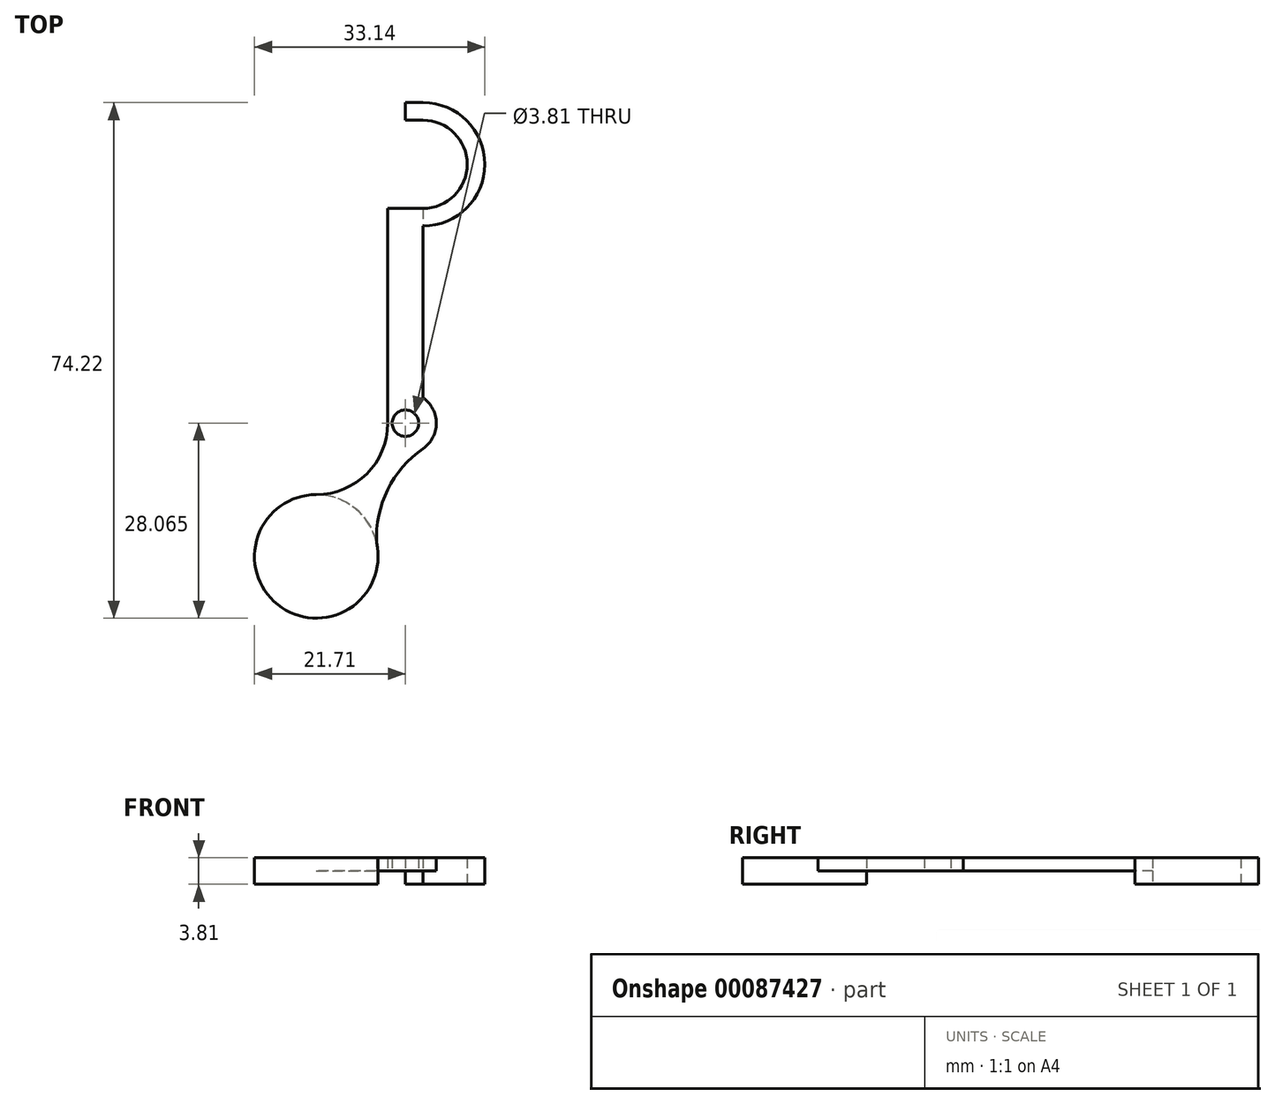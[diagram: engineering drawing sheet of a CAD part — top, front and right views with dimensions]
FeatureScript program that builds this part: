
annotation { "Feature Type Name" : "Feature", "Feature Type Description" : "" }
export const myFeature = defineFeature(function(context is Context, id is Id, definition is map)
    precondition{}
    {
        {
            var Q0;
            Q0=qCreatedBy(makeId("Top.planeOp"),FACE);
            var sketch = newSketch(context, id + "F0", { "sketchPlane" : qUnion([Q0])});
            skLineSegment(sketch, "E0", {"start": v(0, 50.8) * mm, "end": v(0, 0) * mm, "construction": true});
            skLineSegment(sketch, "E1", {"start": v(0, 35.56) * mm, "end": v(0, 0) * mm});
            skPoint(sketch, "E2", {"position": v(-31.04, 0) * mm});
            skCircle(sketch, "E3", {"center": v(-15.36, -11.99) * mm, "radius": 8.9 * mm});
            skLineSegment(sketch, "E4", {"start": v(0, 53.34) * mm, "end": v(0, 50.8) * mm});
            skArc(sketch, "E5", {"start": v(-15.36, -3.1) * mm, "mid": v(-8.1, -0.09) * mm, "end": v(-5.08, 7.19) * mm});
            skArc(sketch, "E6", {"start": v(0, 35.56) * mm, "mid": v(8.89, 44.45) * mm, "end": v(0, 53.34) * mm});
            skArc(sketch, "E7", {"start": v(0, 38.1) * mm, "mid": v(6.35, 44.45) * mm, "end": v(0, 50.8) * mm});
            skLineSegment(sketch, "E8", {"start": v(0, 38.1) * mm, "end": v(0, 35.56) * mm});
            skLineSegment(sketch, "E9", {"start": v(-5.08, 38.1) * mm, "end": v(0, 38.1) * mm});
            skLineSegment(sketch, "E10", {"start": v(-5.08, 38.1) * mm, "end": v(-5.08, 0) * mm});
            skLineSegment(sketch, "E11", {"start": v(0, 3.54) * mm, "end": v(-5.08, 0) * mm, "construction": true});
            skLineSegment(sketch, "E12", {"start": v(0, 53.34) * mm, "end": v(-2.54, 53.34) * mm});
            skLineSegment(sketch, "E13", {"start": v(-2.54, 53.34) * mm, "end": v(-2.54, 50.8) * mm});
            skLineSegment(sketch, "E14", {"start": v(-2.54, 50.8) * mm, "end": v(0, 50.8) * mm});
            skCircle(sketch, "E15", {"center": v(-2.54, 7.19) * mm, "radius": 1.9 * mm});
            skPoint(sketch, "E15.centerSnap0", {"position": v(-2.54, 1.77) * mm});
            skArc(sketch, "E16.0", {"start": v(0, 3.54) * mm, "mid": v(1.9, 7.19) * mm, "end": v(0, 10.83) * mm});
            skArc(sketch, "E17", {"start": v(0, 3.54) * mm, "mid": v(-5.5, -3.28) * mm, "end": v(-6.47, -11.99) * mm});
            skSolve(sketch);
        }
        {
            var Q0;
            Q0 = qSketchRegion(id + "F0", true);
            extrude(context, id + "F1", {"entities" : qUnion([Q0]), "depth" : 3.8 * mm});
        }
        {
            var Q0;
            {var subQ1=sQuery(id+"F0.wireOp",EDGE,"E1");Q0=makeQuery(id+"F0.imprint","IMPRINT",FACE,{"disambiguationData":[TD([[makeQuery(id+"F0.imprint","IMPRINT",EDGE,{"derivedFrom":subQ1}),-1.0]])]});}
            var Q1;
            {var subQ0=sQuery(id+"F0.wireOp",EDGE,"E5");Q1=makeQuery(id+"F0.imprint","IMPRINT",FACE,{"disambiguationData":[TD([[makeQuery(id+"F0.imprint","IMPRINT",EDGE,{"derivedFrom":subQ0}),-1.0]])]});}
            var Q2;
            {var subQ0=sQuery(id+"F0.wireOp",EDGE,"t0VB1PUQ-RfSN-Wfje-U51E-yYEwLlaeleKK");Q2=makeQuery(id+"F0.imprint","IMPRINT",FACE,{"disambiguationData":[TD([[makeQuery(id+"F0.imprint","IMPRINT",EDGE,{"derivedFrom":subQ0}),1.0]])]});}
            var Q3;
            {var subQ0=sQuery(id+"F0.wireOp",EDGE,"E16.0");Q3=makeQuery(id+"F0.imprint","IMPRINT",FACE,{"disambiguationData":[TD([[makeQuery(id+"F0.imprint","IMPRINT",EDGE,{"derivedFrom":subQ0}),1.0]])]});}
            extrude(context, id + "F2", {"entities" : qUnion([Q0, Q1, Q2, Q3]), "operationType" : NewBodyOperationType.REMOVE, "depth" : 1.9 * mm});
        }
    });
